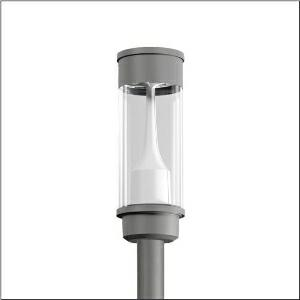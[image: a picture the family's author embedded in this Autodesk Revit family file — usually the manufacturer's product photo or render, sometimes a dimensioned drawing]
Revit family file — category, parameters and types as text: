
# Revit family: litepole_iq___p1_0a_5xa5415nf14h_8c95
name_source: partatom
category: Lighting Fixtures
units: mm (PartAtom-declared; Revit-internal decimal feet)

## family parameters
Cut with Voids When Loaded = No
Host = Face
Light Source = No
Part Type = Normal
Room Calculation Point = No
Round Connector Dimension = Use Diameter
Shared = No

## types (1)
- --- (1 x LED, 1510 lm, 11.8 W, 2700K)
    Apparent Load = 12 VA
    CIE Flux Codes = 32 61 90 93 100
    Color Rendering = 70
    Color Temperature = 2700K
    Default Elevation = 1800 mm
    Description = Litepole iQ, mast luminaire, Module 540 iQ-SR, primary light control with 3 zone facetted reflector, of plastic, silver coated, highly specular, structured, primary optical cover: cover, of PMMA, transparent, partly coated, light distribution: P1.0a, light emission: direct distribution, primary light characteristic: strongly asymmetric, installation type: post-top, LED, High Power LED, rated luminous flux: 1.510lm, luminous efficacy: 128lm/W, light colour: 727, colour temperature: 2700K, control gear: iQ Street-Remote, control: optimised constant luminous flux control (CLO 2.0), Desk-Remote (wireless, voltage-free reading and setting of iQ features in the workshop via application-optimized NFC function/RFID function), Light-Fading, Smart-Wire, Night-Set, Lumen-Switch, Temp-Guard, Auto-Match, Street-Remote, pre-setting: logarithmic dimming characteristic, with terminal, 6-pole, max. 2.5mm², mains connection: 230..240V, AC, 50/60Hz, start of lifetime: 12W, end of service life: 12W, reduction: 6W, luminaire housing, upper part, of glass-fibre reinforced polyester, coated, Siteco® metallic grey (DB 702S), diameter: 210mm, height: 590mm, spigot size: d x l = 76 x 70mm (post-top) | with reducer (optional accessory) 60 x 70mm, mounting height: 3..5m, post-top mast mounting element, of diecast aluminium, coated, Siteco® metallic grey (DB 702S), Module 540 iQ-SR, traffic white (RAL 9016), equipment: standard, protection rating (complete): IP65, insulation class (complete): insulation class II (safety insulation), certification: CE, ENEC, VDE, packaging unit: 1 piece

Light Distribution: P1.0a
    Height = 590 mm
    Lamp = 1 x LED
    Lamp Light Flux = 1510 lm
    Lamp Power = 11.8 W
    Lamp count = 1
    Length = 220 mm
    Luminous efficacy = 128 lm/W
    Manufacturer = Siteco
    ModVariant = No
    Model = 5XA5415NF14H
    Number of Poles = 1
    OnlyDefault = Yes
    Power Factor = 1
    Product Name = Litepole iQ | P1.0a
    Product group = mast luminaire | pylon top
    ProductGroupID = 6100
    Protection Class = Protection class II
    Protection Degree = IP 65
    RLX_Detail_Level = 1
    RLX_Emergency_Light_Flux = 0 lm
    RLX_Emergency_Type = 0
    RLX_Emergency_Type_DB = No
    RlxData = <blob elided: 63893 chars, md5=299b4948>
    Socket = socket
    Standby Power = 0 W
    System Light Flux = 1510 lm
    System Power = 12 W
    Type Comments = factory setting: luminous flux: 100 % | dim-lin: 254 | 472 mA
    Type Image = l_1006025.jpg
    URL = http://relux.com
    VarID = @adj_174471
    Voltage = 0 V
    Weight = 0.00 kg
    Width = 0 mm  [stored 0 ft]

note: [stored X ft] marks values corroborated as IEEE doubles in the binary element streams (Revit-internal decimal feet)

## geometry (parser evidence)
native form markers: Blend x4, Sweep x13
no freeform markers — native parametric forms only
